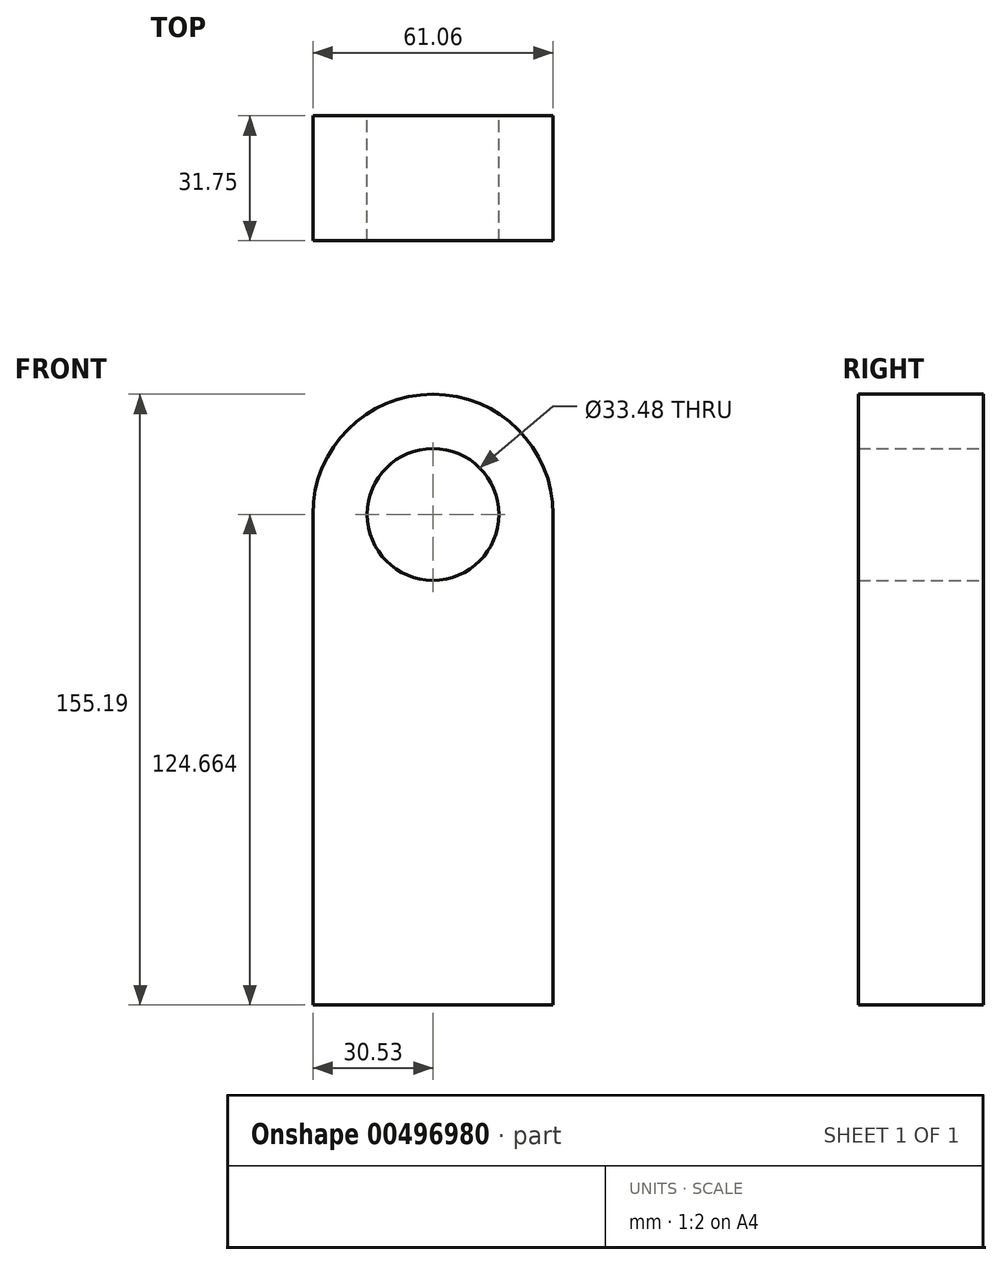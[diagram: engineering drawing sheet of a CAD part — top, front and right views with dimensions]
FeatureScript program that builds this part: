
annotation { "Feature Type Name" : "Feature", "Feature Type Description" : "" }
export const myFeature = defineFeature(function(context is Context, id is Id, definition is map)
    precondition{}
    {
        {
            var Q0;
            Q0=qCreatedBy(makeId("Front.planeOp"),FACE);
            var sketch = newSketch(context, id + "F0", { "sketchPlane" : qUnion([Q0])});
            skLineSegment(sketch, "E0.bottom", {"start": v(30.53, -62.33) * mm, "end": v(-30.53, -62.33) * mm});
            skLineSegment(sketch, "E0.left", {"start": v(30.53, -62.33) * mm, "end": v(30.53, 62.33) * mm});
            skLineSegment(sketch, "E0.right", {"start": v(-30.53, -62.33) * mm, "end": v(-30.53, 62.33) * mm});
            skPoint(sketch, "E0.middle", {"position": v(0, 0) * mm});
            skCircle(sketch, "E1", {"center": v(0, 62.33) * mm, "radius": 30.53 * mm});
            skCircle(sketch, "E2", {"center": v(0, 62.33) * mm, "radius": 16.74 * mm});
            skPoint(sketch, "E3.endSnap0", {"position": v(0, -62.33) * mm});
            skPoint(sketch, "E4.orphan", {"position": v(0, 132.6) * mm});
            skPoint(sketch, "E5.orphan", {"position": v(0, -74.03) * mm});
            skSolve(sketch);
        }
        {
            var Q0;
            Q0=makeQuery(id+"F0.imprint","IMPRINT",FACE,{"disambiguationData":[TD([[makeQuery(id+"F0.imprint","IMPRINT",EDGE,{"derivedFrom":sQuery(id+"F0.wireOp",EDGE,"E0.bottom")}),-1.0]])]});
            var Q1;
            Q1=makeQuery(id+"F0.imprint","IMPRINT",FACE,{"disambiguationData":[TD([[makeQuery(id+"F0.imprint","IMPRINT",EDGE,{"derivedFrom":sQuery(id+"F0.wireOp",EDGE,"E2")}),-1.0]])]});
            extrude(context, id + "F1", {"entities" : qUnion([Q0, Q1]), "depth" : 31.75 * mm});
        }
    });
